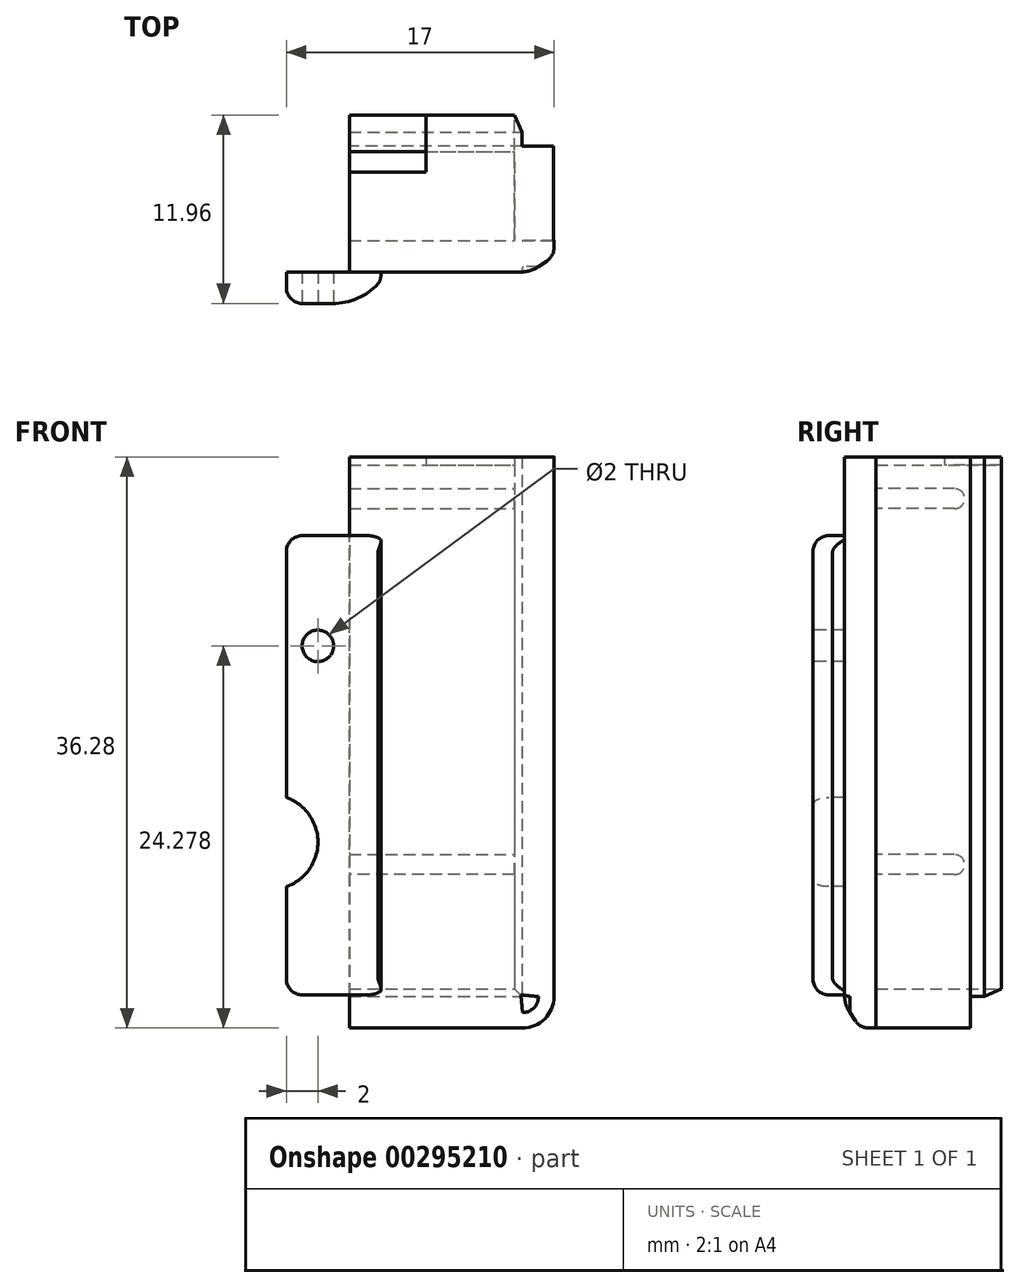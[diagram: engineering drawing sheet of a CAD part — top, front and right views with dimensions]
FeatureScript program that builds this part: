
annotation { "Feature Type Name" : "Feature", "Feature Type Description" : "" }
export const myFeature = defineFeature(function(context is Context, id is Id, definition is map)
    precondition{}
    {
        {
            var Q0;
            Q0=qCreatedBy(makeId("Front.planeOp"),FACE);
            var sketch = newSketch(context, id + "F0", { "sketchPlane" : qUnion([Q0])});
            skLineSegment(sketch, "E0", {"start": v(12.98, 38.01) * mm, "end": v(12.98, 70.29) * mm});
            skLineSegment(sketch, "E1", {"start": v(10.98, 72.29) * mm, "end": v(0, 72.29) * mm});
            skLineSegment(sketch, "E2", {"start": v(0, 72.29) * mm, "end": v(0, 71.79) * mm});
            skLineSegment(sketch, "E3", {"start": v(10.98, 70.29) * mm, "end": v(10.98, 38.01) * mm});
            skPoint(sketch, "E4.visualSharp", {"position": v(12.98, 72.29) * mm});
            skPoint(sketch, "E5.visualSharp", {"position": v(12.98, 0) * mm});
            skPoint(sketch, "E6.start.orphan", {"position": v(0, 2) * mm});
            skLineSegment(sketch, "E7", {"start": v(10.98, 36.01) * mm, "end": v(0, 36.01) * mm});
            skLineSegment(sketch, "E8", {"start": v(0, 36.01) * mm, "end": v(0, 38.01) * mm});
            skLineSegment(sketch, "E9", {"start": v(0, 38.01) * mm, "end": v(10.98, 38.01) * mm});
            skArc(sketch, "E10.filletArc", {"start": v(10.98, 36.01) * mm, "mid": v(12.4, 36.6) * mm, "end": v(12.98, 38.01) * mm});
            skLineSegment(sketch, "E11", {"start": v(12.98, 70.29) * mm, "end": v(12.98, 72.29) * mm});
            skLineSegment(sketch, "E12", {"start": v(12.98, 72.29) * mm, "end": v(10.98, 72.29) * mm});
            skLineSegment(sketch, "E13", {"start": v(0, 71.79) * mm, "end": v(10.98, 71.79) * mm});
            skLineSegment(sketch, "E14", {"start": v(10.98, 71.79) * mm, "end": v(10.98, 70.29) * mm});
            skSolve(sketch);
        }
        {
            var Q0;
            Q0=makeQuery(id+"F0.imprint","IMPRINT",FACE,{"disambiguationData":[TD([[makeQuery(id+"F0.imprint","IMPRINT",EDGE,{"derivedFrom":sQuery(id+"F0.wireOp",EDGE,"E0")}),1.0]])]});
            extrude(context, id + "F1", {"entities" : qUnion([Q0]), "depth" : 6 * mm});
        }
        {
            var Q0;
            Q0=makeQuery(id+"F1.opExtrude","SWEPT_FACE",FACE,{"disambiguationData":[OSD([sQuery(id+"F0.wireOp",EDGE,"E2")])]});
            var sketch = newSketch(context, id + "F2", { "sketchPlane" : qUnion([Q0])});
            skLineSegment(sketch, "E15.bottom", {"start": v(6, 72.29) * mm, "end": v(8, 72.29) * mm});
            skLineSegment(sketch, "E15.left", {"start": v(6, 72.29) * mm, "end": v(6, 36.3) * mm});
            skLineSegment(sketch, "E15.right", {"start": v(8, 72.29) * mm, "end": v(8, 36.3) * mm});
            skLineSegment(sketch, "E16", {"start": v(6, 36.3) * mm, "end": v(6, 36.01) * mm});
            skLineSegment(sketch, "E17", {"start": v(6, 36.01) * mm, "end": v(8, 36.01) * mm});
            skLineSegment(sketch, "E18", {"start": v(8, 36.01) * mm, "end": v(8, 36.3) * mm});
            skSolve(sketch);
        }
        {
            var Q0;
            Q0=qSketchRegion(id+"F2",true);
            extrude(context, id + "F3", {"entities" : qUnion([Q0]), "operationType" : NewBodyOperationType.ADD, "oppositeDirection" : true, "depth" : 13 * mm});
        }
        {
            var Q0;
            Q0=makeQuery(id+"F3.opExtrude","CAP_EDGE",EDGE,{"disambiguationData":[OSD([sQuery(id+"F2.wireOp",EDGE,"E15.top")])],"isStart":false});
            var Q1;
            Q1=makeQuery(id+"F3.opExtrude","CAP_EDGE",EDGE,{"disambiguationData":[OSD([sQuery(id+"F2.wireOp",EDGE,"E17")])],"isStart":false});
            fillet(context, id + "F4", {"entities" : qUnion([Q0, Q1]), "radius" : 2 * mm, "tangentPropagation" : true, "allowEdgeOverflow" : false});
        }
        {
            var Q0;
            Q0=makeQuery(id+"F3.opExtrude","SWEPT_FACE",FACE,{"disambiguationData":[OSD([sQuery(id+"F2.wireOp",EDGE,"E15.right")])]});
            var sketch = newSketch(context, id + "F5", { "sketchPlane" : qUnion([Q0])});
            skLineSegment(sketch, "E19.bottom", {"start": v(2, 67.29) * mm, "end": v(-4, 67.29) * mm});
            skLineSegment(sketch, "E19.top", {"start": v(2, 38.12) * mm, "end": v(-4, 38.12) * mm});
            skLineSegment(sketch, "E19.left", {"start": v(2, 67.29) * mm, "end": v(2, 38.12) * mm});
            skLineSegment(sketch, "E19.right", {"start": v(-4, 67.29) * mm, "end": v(-4, 38.12) * mm});
            skSolve(sketch);
        }
        {
            var Q0;
            Q0=qSketchRegion(id+"F5",true);
            extrude(context, id + "F6", {"entities" : qUnion([Q0]), "operationType" : NewBodyOperationType.ADD, "depth" : 2 * mm});
        }
        {
            var Q0;
            Q0=makeQuery(id+"F6.opExtrude","CAP_EDGE",EDGE,{"disambiguationData":[OSD([sQuery(id+"F5.wireOp",EDGE,"E19.left")])],"isStart":false});
            chamfer(context, id + "F7", {"entities" : qUnion([Q0]), "chamferType" : ChamferType.TWO_OFFSETS, "width1" : 1.5 * mm, "oppositeDirection" : false, "width2" : 1 * mm, "tangentPropagation" : true});
        }
        {
            var Q0;
            {var subQ0=sQuery(id+"F5.wireOp",EDGE,"E19.left");Q0=makeQuery(id+"F7.opChamfer","BLEND_EDGE",EDGE,{"blendedFrom":[makeQuery(id+"F6.opExtrude","CAP_EDGE",EDGE,{"disambiguationData":[OSD([subQ0])],"isStart":false}),makeQuery(id+"F6.opExtrude","SWEPT_FACE",FACE,{"disambiguationData":[OSD([subQ0])]})],"blendedInto":[makeQuery(id+"F6.opExtrude","SWEPT_FACE",FACE,{"disambiguationData":[OSD([subQ0])]})]});}
            fillet(context, id + "F8", {"entities" : qUnion([Q0]), "radius" : 1 * mm, "tangentPropagation" : true, "allowEdgeOverflow" : false});
        }
        {
            var Q0;
            Q0=makeQuery(id+"F6.opExtrude","CAP_FACE",FACE,{"disambiguationData":[OSD([sQuery(id+"F5.wireOp",EDGE,"E19.bottom"),sQuery(id+"F5.wireOp",EDGE,"E19.top"),sQuery(id+"F5.wireOp",EDGE,"E19.left"),sQuery(id+"F5.wireOp",EDGE,"E19.right")])],"isStart":false});
            var sketch = newSketch(context, id + "F9", { "sketchPlane" : qUnion([Q0])});
            skCircle(sketch, "E20", {"center": v(-2, 60.29) * mm, "radius": 1 * mm});
            skSolve(sketch);
        }
        {
            var Q0;
            Q0=qSketchRegion(id+"F9",true);
            extrude(context, id + "F10", {"entities" : qUnion([Q0]), "operationType" : NewBodyOperationType.REMOVE, "oppositeDirection" : true, "depth" : 25 * mm});
        }
        {
            var Q0;
            {var subQ0=sQuery(id+"F5.wireOp",EDGE,"E19.left");Q0=makeQuery(id+"F7.opChamfer","BLEND_EDGE",EDGE,{"blendedFrom":[makeQuery(id+"F6.opExtrude","CAP_EDGE",EDGE,{"disambiguationData":[OSD([subQ0])],"isStart":false}),makeQuery(id+"F6.opExtrude","CAP_FACE",FACE,{"disambiguationData":[OSD([sQuery(id+"F5.wireOp",EDGE,"E19.bottom"),sQuery(id+"F5.wireOp",EDGE,"E19.top"),subQ0,sQuery(id+"F5.wireOp",EDGE,"E19.right")])],"isStart":false})],"blendedInto":[makeQuery(id+"F6.opExtrude","CAP_FACE",FACE,{"disambiguationData":[OSD([sQuery(id+"F5.wireOp",EDGE,"E19.bottom"),sQuery(id+"F5.wireOp",EDGE,"E19.top"),subQ0,sQuery(id+"F5.wireOp",EDGE,"E19.right")])],"isStart":false})]});}
            fillet(context, id + "F11", {"entities" : qUnion([Q0]), "radius" : 4 * mm, "tangentPropagation" : true, "allowEdgeOverflow" : false});
        }
        {
            var Q0;
            Q0=makeQuery(id+"F6.opExtrude","CAP_EDGE",EDGE,{"disambiguationData":[OSD([sQuery(id+"F5.wireOp",EDGE,"E19.top")])],"isStart":false});
            var Q1;
            Q1=makeQuery(id+"F6.opExtrude","CAP_EDGE",EDGE,{"disambiguationData":[OSD([sQuery(id+"F5.wireOp",EDGE,"E19.bottom")])],"isStart":false});
            fillet(context, id + "F12", {"entities" : qUnion([Q0, Q1]), "radius" : 1 * mm, "tangentPropagation" : true, "allowEdgeOverflow" : false});
        }
        {
            var Q0;
            Q0=makeQuery(id+"F6.opExtrude","CAP_EDGE",EDGE,{"disambiguationData":[OSD([sQuery(id+"F5.wireOp",EDGE,"E19.right")])],"isStart":false});
            fillet(context, id + "F13", {"entities" : qUnion([Q0]), "radius" : 1 * mm, "tangentPropagation" : true, "allowEdgeOverflow" : false});
        }
        {
            var Q0;
            Q0=makeQuery(id+"F1.opExtrude","CAP_FACE",FACE,{"disambiguationData":[OSD([sQuery(id+"F0.wireOp",EDGE,"E0"),sQuery(id+"F0.wireOp",EDGE,"E1"),sQuery(id+"F0.wireOp",EDGE,"E2"),sQuery(id+"F0.wireOp",EDGE,"5GWelT8N-WT9G-pHX5-dFQZ-JpsdUA8wokHI"),sQuery(id+"F0.wireOp",EDGE,"E3"),sQuery(id+"F0.wireOp",EDGE,"E4.filletArc"),sQuery(id+"F0.wireOp",EDGE,"SL8cM0Mj-z6Pg-xHqj-tJNP-eVUlfgKiLkpK")])],"isStart":true});
            var sketch = newSketch(context, id + "F14", { "sketchPlane" : qUnion([Q0])});
            skLineSegment(sketch, "E21.left", {"start": v(-10.98, 38.01) * mm, "end": v(-10.98, 38.01) * mm});
            skLineSegment(sketch, "E21.right", {"start": v(-10.48, 70.29) * mm, "end": v(-10.48, 38.51) * mm});
            skLineSegment(sketch, "E22.bottom", {"start": v(-10.98, 72.29) * mm, "end": v(0, 72.29) * mm});
            skLineSegment(sketch, "E22.top", {"start": v(-10.48, 71.79) * mm, "end": v(0, 71.79) * mm});
            skLineSegment(sketch, "E22.left", {"start": v(-10.98, 72.29) * mm, "end": v(-10.98, 71.79) * mm});
            skLineSegment(sketch, "E22.right", {"start": v(0, 72.29) * mm, "end": v(0, 71.79) * mm});
            skLineSegment(sketch, "E23.bottom", {"start": v(-10.98, 72.29) * mm, "end": v(-10.48, 72.29) * mm});
            skLineSegment(sketch, "E23.left", {"start": v(-10.98, 72.29) * mm, "end": v(-10.98, 69.79) * mm});
            skLineSegment(sketch, "E23.right", {"start": v(-10.48, 71.79) * mm, "end": v(-10.48, 38.01) * mm});
            skLineSegment(sketch, "E24.bottom", {"start": v(0, 38.01) * mm, "end": v(-10.98, 38.01) * mm});
            skLineSegment(sketch, "E24.top", {"start": v(0, 38.51) * mm, "end": v(-10.48, 38.51) * mm});
            skLineSegment(sketch, "E24.left", {"start": v(0, 38.01) * mm, "end": v(0, 38.51) * mm});
            skLineSegment(sketch, "E24.right", {"start": v(-10.98, 38.01) * mm, "end": v(-10.98, 38.51) * mm});
            skLineSegment(sketch, "E25", {"start": v(-10.98, 38.51) * mm, "end": v(-10.98, 69.79) * mm});
            skSolve(sketch);
        }
        {
            var Q0;
            Q0=qSketchRegion(id+"F14",true);
            extrude(context, id + "F15", {"entities" : qUnion([Q0]), "operationType" : NewBodyOperationType.ADD, "oppositeDirection" : true, "depth" : 6.1 * mm, "hasSecondDirection" : true, "secondDirectionOppositeDirection" : false, "secondDirectionDepth" : 1.97 * mm});
        }
        {
            var Q0;
            Q0=makeQuery(id+"F15.opExtrude","CAP_EDGE",EDGE,{"disambiguationData":[OSD([sQuery(id+"F14.wireOp",EDGE,"E23.left"),sQuery(id+"F14.wireOp",EDGE,"E24.right"),sQuery(id+"F14.wireOp",EDGE,"E25")])],"isStart":true});
            var Q1;
            Q1=makeQuery(id+"F15.opExtrude","CAP_EDGE",EDGE,{"disambiguationData":[OSD([sQuery(id+"F14.wireOp",EDGE,"E24.bottom")])],"isStart":true});
            chamfer(context, id + "F16", {"entities" : qUnion([Q0, Q1]), "chamferType" : ChamferType.OFFSET_ANGLE, "width" : 0.5 * mm, "oppositeDirection" : false, "angle" : 65 * degree, "tangentPropagation" : true});
        }
        {
            var Q0;
            {var subQ1=sQuery(id+"F2.wireOp",EDGE,"E15.left");Q0=makeQuery(id+"F3.boolean.opBoolean","SPLIT",FACE,{"disambiguationData":[TD([makeQuery(id+"F1.opExtrude","SWEPT_FACE",FACE,{"disambiguationData":[OSD([sQuery(id+"F0.wireOp",EDGE,"E2")])]})])],"derivedFrom":makeQuery(id+"F3.opExtrude","SWEPT_FACE",FACE,{"disambiguationData":[OSD([subQ1])]})});}
            var sketch = newSketch(context, id + "F17", { "sketchPlane" : qUnion([Q0])});
            skLineSegment(sketch, "E26", {"start": v(-10.48, 45.76) * mm, "end": v(-7.39, 45.76) * mm});
            skLineSegment(sketch, "E27", {"start": v(-10.48, 47.03) * mm, "end": v(-7.39, 47.03) * mm});
            skLineSegment(sketch, "E28", {"start": v(-7.39, 45.76) * mm, "end": v(0, 45.76) * mm});
            skLineSegment(sketch, "E29", {"start": v(0, 45.76) * mm, "end": v(0, 47.03) * mm});
            skLineSegment(sketch, "E30", {"start": v(0, 47.03) * mm, "end": v(-7.39, 47.03) * mm});
            skLineSegment(sketch, "E31.bottom", {"start": v(0, 70.28) * mm, "end": v(-10.48, 70.28) * mm});
            skLineSegment(sketch, "E31.top", {"start": v(0, 69) * mm, "end": v(-10.48, 69) * mm});
            skLineSegment(sketch, "E31.left", {"start": v(0, 70.28) * mm, "end": v(0, 69) * mm});
            skLineSegment(sketch, "E31.right", {"start": v(-10.48, 70.28) * mm, "end": v(-10.48, 69) * mm});
            skSolve(sketch);
        }
        {
            var Q0;
            {var subQ0=sQuery(id+"F17.wireOp",EDGE,"E26");Q0=makeQuery(id+"F17.imprint","IMPRINT",FACE,{"disambiguationData":[TD([[makeQuery(id+"F17.imprint","IMPRINT",EDGE,{"derivedFrom":subQ0}),1.0]])]});}
            var Q1;
            Q1=makeQuery(id+"F17.imprint","IMPRINT",FACE,{"disambiguationData":[TD([[makeQuery(id+"F17.imprint","IMPRINT",EDGE,{"derivedFrom":sQuery(id+"F17.wireOp",EDGE,"E31.bottom")}),1.0]])]});
            extrude(context, id + "F18", {"entities" : qUnion([Q0, Q1]), "operationType" : NewBodyOperationType.ADD, "depth" : 5.63 * mm});
        }
        {
            var Q0;
            Q0=makeQuery(id+"F18.opExtrude","CAP_EDGE",EDGE,{"disambiguationData":[OSD([sQuery(id+"F17.wireOp",EDGE,"E26")])],"isStart":false});
            var Q1;
            Q1=makeQuery(id+"F18.opExtrude","CAP_EDGE",EDGE,{"disambiguationData":[OSD([sQuery(id+"F17.wireOp",EDGE,"E27")])],"isStart":false});
            var Q2;
            Q2=makeQuery(id+"F18.opExtrude","CAP_EDGE",EDGE,{"disambiguationData":[OSD([sQuery(id+"F17.wireOp",EDGE,"E31.top")])],"isStart":false});
            var Q3;
            Q3=makeQuery(id+"F18.opExtrude","CAP_EDGE",EDGE,{"disambiguationData":[OSD([sQuery(id+"F17.wireOp",EDGE,"E31.bottom")])],"isStart":false});
            fillet(context, id + "F19", {"entities" : qUnion([Q0, Q1, Q2, Q3]), "radius" : 0.64 * mm, "tangentPropagation" : true, "allowEdgeOverflow" : false});
        }
        {
            var Q0;
            Q0=makeQuery(id+"F3.opExtrude","SWEPT_EDGE",EDGE,{"disambiguationData":[OSD([sQuery(id+"F2.wireOp",EDGE,"E17"),sQuery(id+"F2.wireOp",EDGE,"E18")])]});
            chamfer(context, id + "F20", {"entities" : qUnion([Q0]), "chamferType" : ChamferType.TWO_OFFSETS, "width1" : 1 * mm, "oppositeDirection" : false, "width2" : 1.5 * mm, "tangentPropagation" : true});
        }
        {
            var Q0;
            {var subQ0=sQuery(id+"F2.wireOp",EDGE,"E18");Q0=makeQuery(id+"F20.opChamfer","BLEND_EDGE",EDGE,{"blendedFrom":[makeQuery(id+"F3.opExtrude","SWEPT_EDGE",EDGE,{"disambiguationData":[OSD([sQuery(id+"F2.wireOp",EDGE,"E17"),subQ0])]}),makeQuery(id+"F3.opExtrude","SWEPT_FACE",FACE,{"disambiguationData":[OSD([sQuery(id+"F2.wireOp",EDGE,"E15.right"),subQ0])]})],"blendedInto":[makeQuery(id+"F3.opExtrude","SWEPT_FACE",FACE,{"disambiguationData":[OSD([sQuery(id+"F2.wireOp",EDGE,"E15.right"),subQ0])]})]});}
            fillet(context, id + "F21", {"entities" : qUnion([Q0]), "radius" : 2 * mm, "tangentPropagation" : true, "allowEdgeOverflow" : false});
        }
        {
            var Q0;
            {var subQ0=sQuery(id+"F2.wireOp",EDGE,"E17");Q0=makeQuery(id+"F20.opChamfer","BLEND_EDGE",EDGE,{"blendedFrom":[makeQuery(id+"F3.opExtrude","SWEPT_EDGE",EDGE,{"disambiguationData":[OSD([subQ0,sQuery(id+"F2.wireOp",EDGE,"E18")])]}),makeQuery(id+"F3.boolean.opBoolean","MERGE",FACE,{"derivedFrom":[makeQuery(id+"F1.opExtrude","SWEPT_FACE",FACE,{"disambiguationData":[OSD([sQuery(id+"F0.wireOp",EDGE,"E7")])]}),makeQuery(id+"F3.opExtrude","SWEPT_FACE",FACE,{"disambiguationData":[OSD([subQ0])]})]})],"blendedInto":[makeQuery(id+"F3.boolean.opBoolean","MERGE",FACE,{"derivedFrom":[makeQuery(id+"F1.opExtrude","SWEPT_FACE",FACE,{"disambiguationData":[OSD([sQuery(id+"F0.wireOp",EDGE,"E7")])]}),makeQuery(id+"F3.opExtrude","SWEPT_FACE",FACE,{"disambiguationData":[OSD([subQ0])]})]})]});}
            fillet(context, id + "F22", {"entities" : qUnion([Q0]), "radius" : 1 * mm, "tangentPropagation" : true, "allowEdgeOverflow" : false});
        }
        {
            var Q0;
            Q0=makeQuery(id+"F15.boolean.opBoolean","MERGE",FACE,{"derivedFrom":[makeQuery(id+"F1.opExtrude","SWEPT_FACE",FACE,{"disambiguationData":[OSD([sQuery(id+"F0.wireOp",EDGE,"E13")])]}),makeQuery(id+"F15.opExtrude","SWEPT_FACE",FACE,{"disambiguationData":[OSD([sQuery(id+"F14.wireOp",EDGE,"E22.top")])]})]});
            var sketch = newSketch(context, id + "F23", { "sketchPlane" : qUnion([Q0])});
            skLineSegment(sketch, "E32.bottom", {"start": v(0, -1.97) * mm, "end": v(4.88, -1.97) * mm});
            skLineSegment(sketch, "E32.top", {"start": v(0, 1.64) * mm, "end": v(4.88, 1.64) * mm});
            skLineSegment(sketch, "E32.left", {"start": v(0, -1.97) * mm, "end": v(0, 1.64) * mm});
            skLineSegment(sketch, "E32.right", {"start": v(4.88, -1.97) * mm, "end": v(4.88, 1.64) * mm});
            skSolve(sketch);
        }
        {
            var Q0;
            Q0 = qSketchRegion(id + "F23", true);
            extrude(context, id + "F24", {"entities" : qUnion([Q0]), "operationType" : NewBodyOperationType.REMOVE, "oppositeDirection" : true, "depth" : 25 * mm});
        }
        {
            var Q0;
            Q0=makeQuery(id+"F13.opFillet","SPLIT",FACE,{"disambiguationData":[OD(1.0)],"derivedFrom":makeQuery(id+"F6.opExtrude","CAP_FACE",FACE,{"disambiguationData":[OSD([sQuery(id+"F5.wireOp",EDGE,"E19.bottom"),sQuery(id+"F5.wireOp",EDGE,"E19.top"),sQuery(id+"F5.wireOp",EDGE,"E19.left"),sQuery(id+"F5.wireOp",EDGE,"E19.right")])],"isStart":false})});
            var sketch = newSketch(context, id + "F25", { "sketchPlane" : qUnion([Q0])});
            skCircle(sketch, "E33", {"center": v(-5, 47.82) * mm, "radius": 3 * mm});
            skSolve(sketch);
        }
        {
            var Q0;
            Q0 = qSketchRegion(id + "F25", true);
            extrude(context, id + "F26", {"entities" : qUnion([Q0]), "operationType" : NewBodyOperationType.REMOVE, "oppositeDirection" : true, "depth" : 25 * mm});
        }
    });
